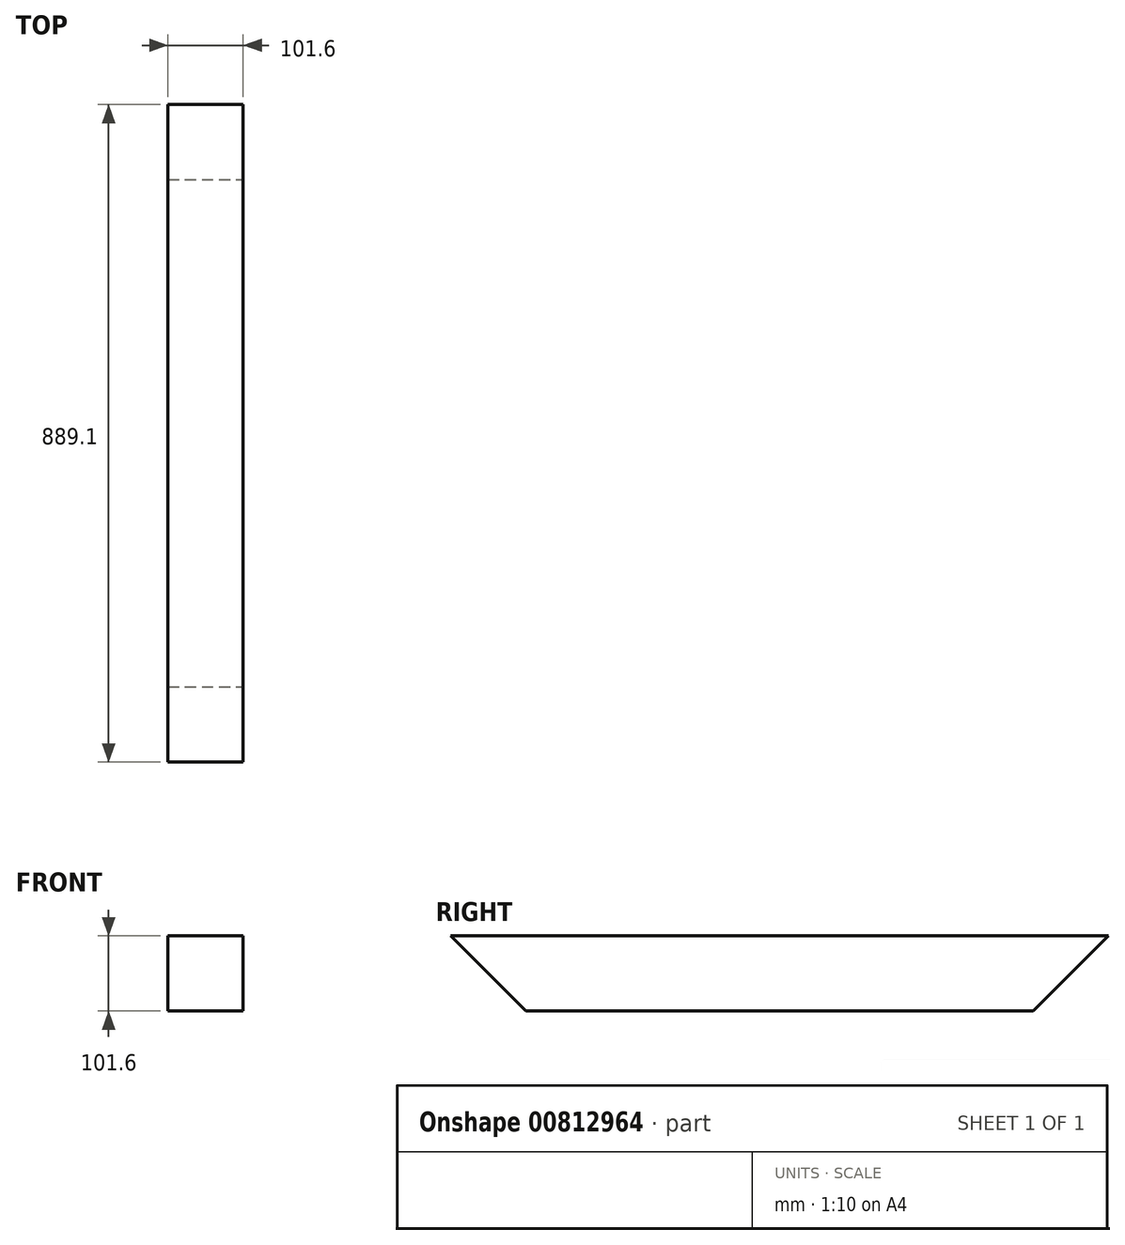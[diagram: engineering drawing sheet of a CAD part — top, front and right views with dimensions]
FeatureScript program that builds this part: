
annotation { "Feature Type Name" : "Feature", "Feature Type Description" : "" }
export const myFeature = defineFeature(function(context is Context, id is Id, definition is map)
    precondition{}
    {
        {
            var Q0;
            Q0=qCreatedBy(makeId("Front.planeOp"),FACE);
            var sketch = newSketch(context, id + "F0", { "sketchPlane" : qUnion([Q0])});
            skLineSegment(sketch, "E0.bottom", {"start": v(50.8, 50.8) * mm, "end": v(-50.8, 50.8) * mm});
            skLineSegment(sketch, "E0.top", {"start": v(50.8, -50.8) * mm, "end": v(-50.8, -50.8) * mm});
            skLineSegment(sketch, "E0.left", {"start": v(50.8, 50.8) * mm, "end": v(50.8, -50.8) * mm});
            skLineSegment(sketch, "E0.right", {"start": v(-50.8, 50.8) * mm, "end": v(-50.8, -50.8) * mm});
            skPoint(sketch, "E0.middle", {"position": v(0, 0) * mm});
            skSolve(sketch);
        }
        {
            var Q0;
            Q0 = qSketchRegion(id + "F0", true);
            extrude(context, id + "F1", {"entities" : qUnion([Q0]), "depth" : 889.1 * mm, "offsetDistance" : 25.4 * mm, "symmetric" : true});
        }
        {
            var Q0;
            Q0=makeQuery(id+"F1.opExtrude","SWEPT_FACE",FACE,{"disambiguationData":[OSD([sQuery(id+"F0.wireOp",EDGE,"E0.left")])]});
            var sketch = newSketch(context, id + "F2", { "sketchPlane" : qUnion([Q0])});
            skLineSegment(sketch, "E1", {"start": v(-444.55, -50.8) * mm, "end": v(-444.55, 50.8) * mm});
            skLineSegment(sketch, "E2", {"start": v(444.55, 50.8) * mm, "end": v(342.95, -50.8) * mm});
            skLineSegment(sketch, "E3", {"start": v(342.95, -50.8) * mm, "end": v(444.55, -50.8) * mm});
            skLineSegment(sketch, "E4", {"start": v(444.55, -50.8) * mm, "end": v(444.55, 50.8) * mm});
            skLineSegment(sketch, "E5", {"start": v(-444.55, 50.8) * mm, "end": v(-342.95, -50.8) * mm});
            skLineSegment(sketch, "E6", {"start": v(-342.95, -50.8) * mm, "end": v(-444.55, -50.8) * mm});
            skSolve(sketch);
        }
        {
            var Q0;
            Q0 = qSketchRegion(id + "F2", true);
            extrude(context, id + "F3", {"entities" : qUnion([Q0]), "operationType" : NewBodyOperationType.REMOVE, "endBound" : BoundingType.THROUGH_ALL, "oppositeDirection" : true, "depth" : 25.4 * mm, "offsetDistance" : 25.4 * mm});
        }
    });
